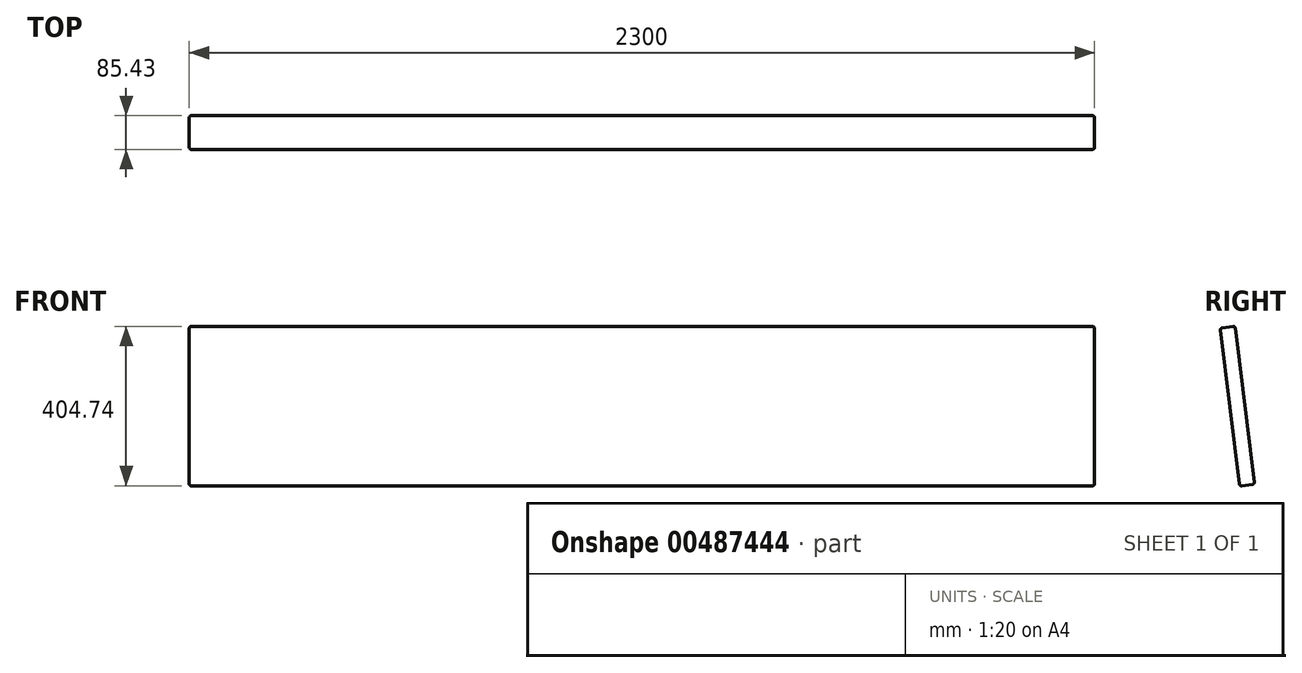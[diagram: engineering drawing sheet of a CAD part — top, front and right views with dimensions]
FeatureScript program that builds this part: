
annotation { "Feature Type Name" : "Feature", "Feature Type Description" : "" }
export const myFeature = defineFeature(function(context is Context, id is Id, definition is map)
    precondition{}
    {
        {
            var Q0;
            Q0=qCreatedBy(makeId("Right.planeOp"),FACE);
            var sketch = newSketch(context, id + "F0", { "sketchPlane" : qUnion([Q0])});
            skLineSegment(sketch, "E0", {"start": v(105.04, 913.57) * mm, "end": v(153.1, 522.2) * mm});
            skLineSegment(sketch, "E1", {"start": v(158.67, 517.84) * mm, "end": v(186.05, 521.2) * mm});
            skLineSegment(sketch, "E2", {"start": v(190.4, 526.77) * mm, "end": v(142.35, 918.15) * mm});
            skLineSegment(sketch, "E3", {"start": v(109.4, 919.14) * mm, "end": v(136.78, 922.5) * mm});
            skPoint(sketch, "E4.visualSharp", {"position": v(104.44, 918.53) * mm});
            skArc(sketch, "E4.filletArc", {"start": v(109.4, 919.14) * mm, "mid": v(106.07, 917.25) * mm, "end": v(105.04, 913.57) * mm});
            skPoint(sketch, "E5.visualSharp", {"position": v(141.74, 923.11) * mm});
            skArc(sketch, "E5.filletArc", {"start": v(142.35, 918.15) * mm, "mid": v(140.46, 921.48) * mm, "end": v(136.78, 922.5) * mm});
            skPoint(sketch, "E6.visualSharp", {"position": v(153.7, 517.23) * mm});
            skArc(sketch, "E6.filletArc", {"start": v(153.1, 522.2) * mm, "mid": v(154.98, 518.86) * mm, "end": v(158.67, 517.84) * mm});
            skPoint(sketch, "E7.visualSharp", {"position": v(191.01, 521.8) * mm});
            skArc(sketch, "E7.filletArc", {"start": v(186.05, 521.2) * mm, "mid": v(189.38, 523.08) * mm, "end": v(190.4, 526.77) * mm});
            skSolve(sketch);
        }
        {
            var Q0;
            Q0 = qSketchRegion(id + "F0", true);
            extrude(context, id + "F1", {"entities" : qUnion([Q0]), "oppositeDirection" : true, "depth" : 2300 * mm});
        }
        {
            var Q0;
            Q0=makeQuery(id+"F1.opExtrude","CAP_FACE",FACE,{"disambiguationData":[OSD([sQuery(id+"F0.wireOp",EDGE,"E0"),sQuery(id+"F0.wireOp",EDGE,"E1"),sQuery(id+"F0.wireOp",EDGE,"E2"),sQuery(id+"F0.wireOp",EDGE,"E3"),sQuery(id+"F0.wireOp",EDGE,"E4.filletArc"),sQuery(id+"F0.wireOp",EDGE,"E5.filletArc"),sQuery(id+"F0.wireOp",EDGE,"E6.filletArc"),sQuery(id+"F0.wireOp",EDGE,"E7.filletArc")])],"isStart":true});
            fillet(context, id + "F2", {"entities" : qUnion([Q0]), "radius" : 5 * mm, "tangentPropagation" : true, "allowEdgeOverflow" : false});
        }
        {
            var Q0;
            Q0=makeQuery(id+"F1.opExtrude","CAP_FACE",FACE,{"disambiguationData":[OSD([sQuery(id+"F0.wireOp",EDGE,"E0"),sQuery(id+"F0.wireOp",EDGE,"E1"),sQuery(id+"F0.wireOp",EDGE,"E2"),sQuery(id+"F0.wireOp",EDGE,"E3"),sQuery(id+"F0.wireOp",EDGE,"E4.filletArc"),sQuery(id+"F0.wireOp",EDGE,"E5.filletArc"),sQuery(id+"F0.wireOp",EDGE,"E6.filletArc"),sQuery(id+"F0.wireOp",EDGE,"E7.filletArc")])],"isStart":false});
            fillet(context, id + "F3", {"entities" : qUnion([Q0]), "radius" : 5 * mm, "tangentPropagation" : true, "allowEdgeOverflow" : false});
        }
    });
